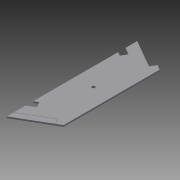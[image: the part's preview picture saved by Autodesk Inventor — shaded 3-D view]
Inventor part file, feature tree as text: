
AUTODESK INVENTOR PART (.ipt)
format: ipt  version: 2015 SP1 (Build 190203100, 203)  size: 130,048 bytes
history: native  units: in
note: dims shown in document units (in); Inventor stores cm internally (conversion verified against a paired STEP export)
features: reference x4, sketch x3, extrude x2, hole x1
ambient origin geometry x8: Origin, YZ Plane, XZ Plane, XY Plane, X Axis, Y Axis, Z Axis, Center Point
bodies: Solid1 (feature_tree)
feature tree (10):
  extrude  "Extrusion1"  TaperAngle=30.0deg  [1 undecoded]
  hole  "Hole1"  [1 undecoded]
  extrude  "Extrusion3"  Depth=3.0in
  sketch  "Sketch1"  dims[d0=120.0deg d1=30.0deg]
  sketch  "Sketch4"  dims[d2=16.0in d3=0.25in d4=0.0in]
  sketch  "Sketch5"  dims[d5=6.0in d12=3.0in d13=8.0in d14=0.5312in d15=0.75in d16=0.375in d17=0.25in d18=0.5635in d19=1.0in d20=0.8108in d22=0.04in d23=0.04in d24=0.04in d25=0.04in d26=1.0in d27=0.0in]
  reference  "Reference10"
  reference  "Reference11"
  reference  "Reference12"
  reference  "Reference13"
note: 2 required parameter values undecoded (feature->parameter linkage not recoverable at this tier; creation-order binding heuristic only, values carry confidence <= 0.55)
